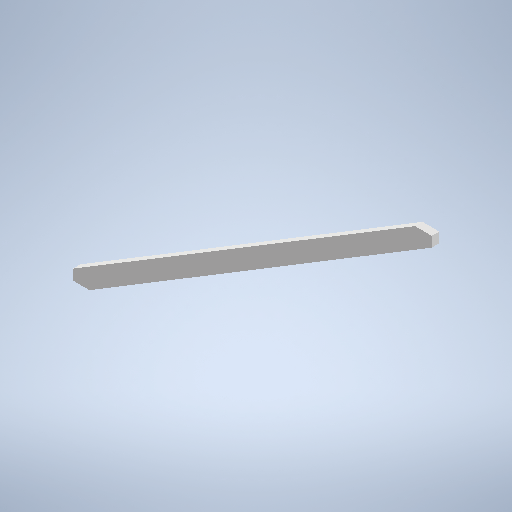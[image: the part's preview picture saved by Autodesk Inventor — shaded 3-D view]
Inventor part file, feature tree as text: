
AUTODESK INVENTOR PART (.ipt)
format: ipt  version: 2025.1 (Build 291241020, 241B)  size: 249,344 bytes
history: native  units: in
note: dims shown in document units (in); Inventor stores cm internally (conversion verified against a paired STEP export)
features: other x6, reference x4, extrude x1, sketch x1
ambient origin geometry x8: Origin, YZ Plane, XZ Plane, XY Plane, X Axis, Y Axis, Z Axis, Center Point
bodies: Solid1 (feature_tree)
feature tree (12):
  extrude  "Extrusion1"  [1 undecoded]
  sketch  "Sketch1"  dims[d2=1.5in d3=0.0in]
  reference  "Reference1"
  reference  "Reference2"
  reference  "Reference3"
  reference  "Reference4"
  other  "<userpath>\Documents\Tburn24\Assembly1.iam"
  other  "Assembly1.iam"
  other  "6'x2x4:1"
  other  "16'x4x4:1"
  other  "16'x2x4:2"
  other  "6'x4x4:18"
note: 1 required parameter value undecoded (feature->parameter linkage not recoverable at this tier; creation-order binding heuristic only, values carry confidence <= 0.55)
